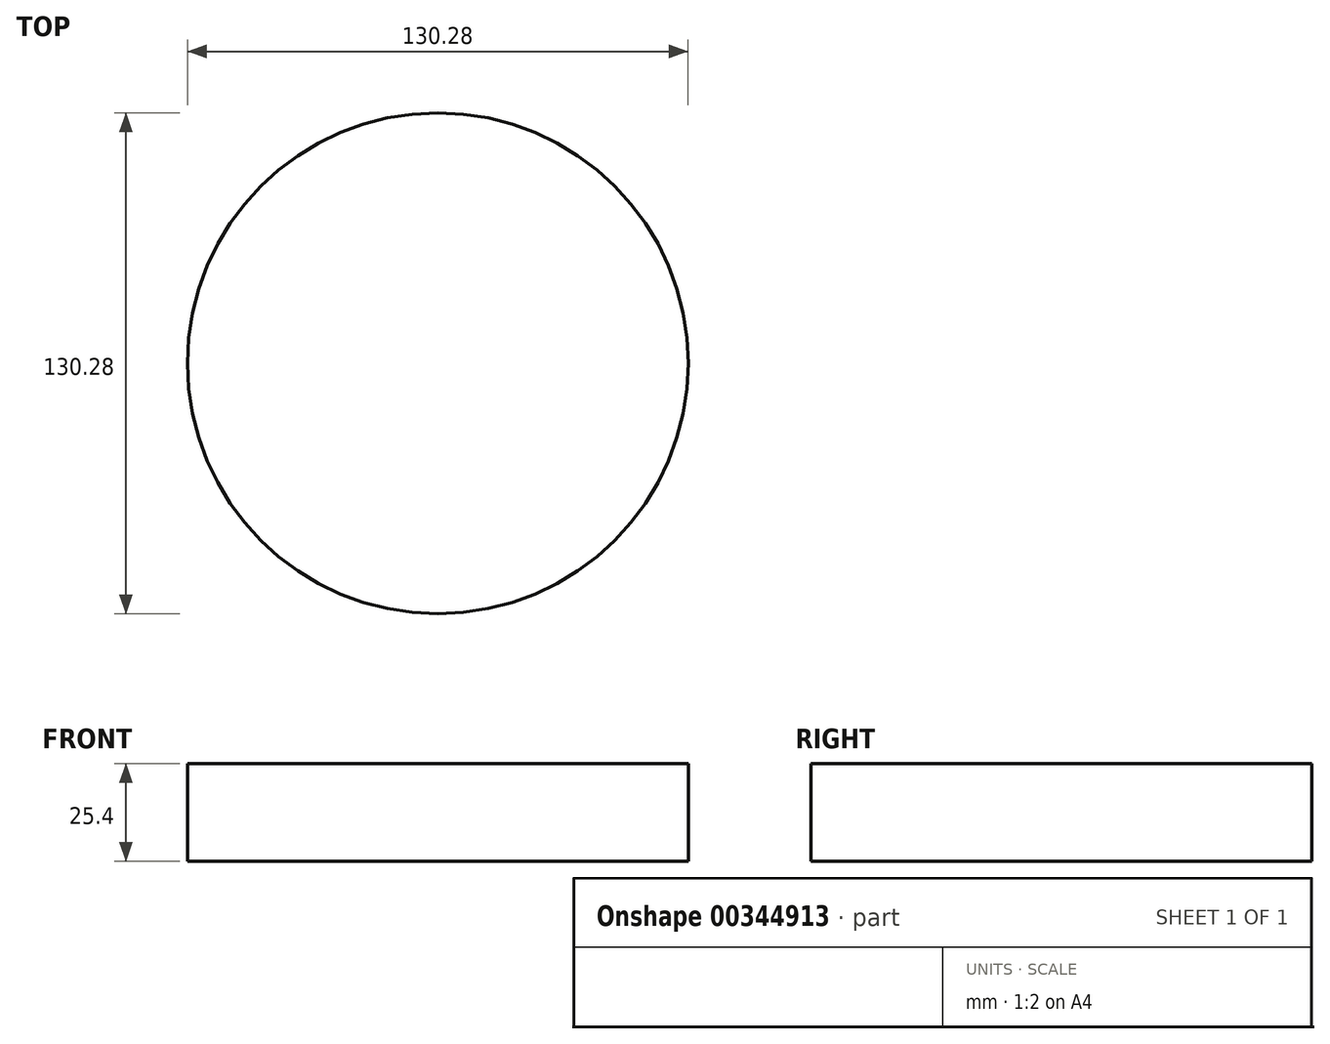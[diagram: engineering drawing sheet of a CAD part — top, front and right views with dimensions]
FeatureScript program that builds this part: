
annotation { "Feature Type Name" : "Feature", "Feature Type Description" : "" }
export const myFeature = defineFeature(function(context is Context, id is Id, definition is map)
    precondition{}
    {
        {
            var Q0;
            Q0=qCreatedBy(makeId("Top.planeOp"),FACE);
            var sketch = newSketch(context, id + "F0", { "sketchPlane" : qUnion([Q0])});
            skCircle(sketch, "E0", {"center": v(2.9, 0) * mm, "radius": 65.14 * mm});
            skSolve(sketch);
        }
        {
            var Q0;
            Q0=makeQuery(id+"F0.imprint","IMPRINT",FACE,{"disambiguationData":[TD([[makeQuery(id+"F0.imprint","IMPRINT",EDGE,{"derivedFrom":sQuery(id+"F0.wireOp",EDGE,"E0")}),1.0]])]});
            extrude(context, id + "F1", {"entities" : qUnion([Q0]), "depth" : 25.4 * mm});
        }
    });
